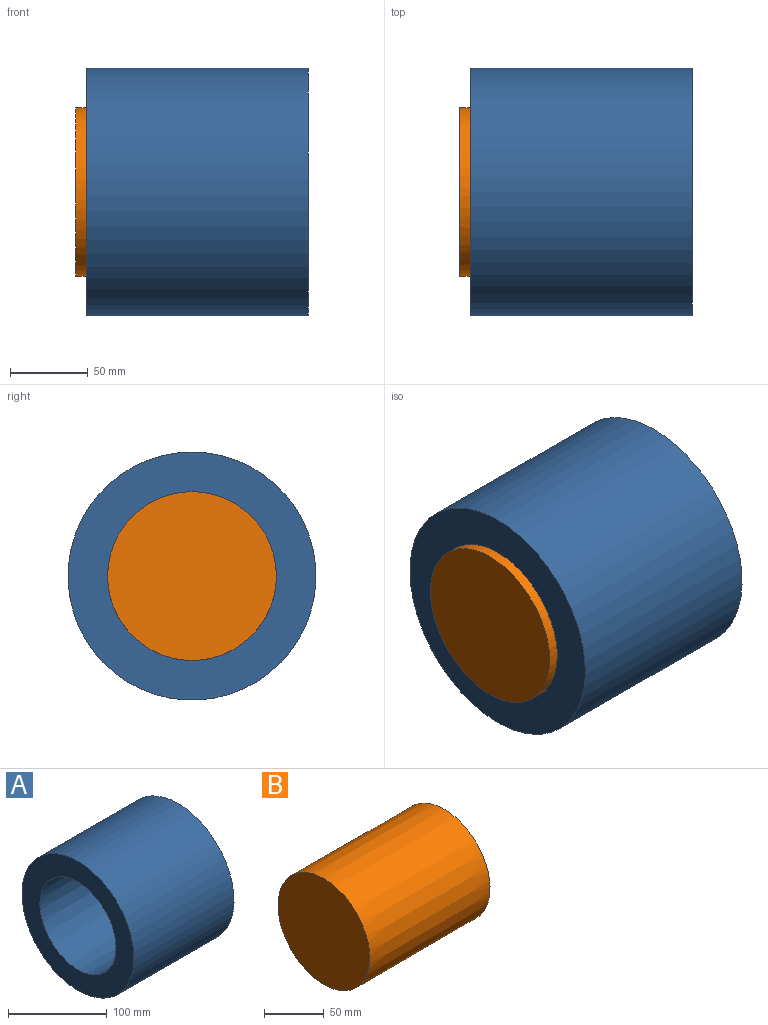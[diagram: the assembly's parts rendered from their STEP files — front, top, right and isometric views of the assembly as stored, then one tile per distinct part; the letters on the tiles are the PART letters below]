
ASSEMBLY  parts=2 mates=1
PART A: 5 faces, bbox 143x160x160 mm
  f0: cylinder r=80mm len=160mm, axis (-1,0,0), area 71879.6mm2, adj f1,f3
  f1: plane 160x160mm, normal (-1,0,0), area 10806.5mm2, adj f0,f2
  f2: cone r=53.93mm half-angle=0.2deg, axis (-1,0,0), area 47993.3mm2, adj f1,f4
  f3: plane 160x160mm, normal (1,0,0), area 10278.4mm2, adj f0,f4
  f4: cone r=55.93mm half-angle=44.9deg, axis (1,0,0), area 974.6mm2, adj f2,f3
PART B: 11 faces, bbox 143x108.8x108.8 mm
  f0: plane 108.83x108.83mm, normal (-1,0,0), area 9301.9mm2, adj f2
  f1: plane 107.91x107.91mm, normal (1,0,0), area 8831.1mm2, adj f2,f3,f5,f7,f9
  f2: cone r=54.41mm half-angle=0.2deg, axis (-1,0,0), area 48684.1mm2, adj f0,f1
  f3: cylinder r=5mm len=30mm, axis (1,0,0), area 942.5mm2, adj f1,f4
  f4: plane 10x10mm, normal (1,0,0), area 78.5mm2, adj f3
  f5: cylinder r=5mm len=30mm, axis (1,0,0), area 942.5mm2, adj f1,f6
  f6: plane 10x10mm, normal (1,0,0), area 78.5mm2, adj f5
  f7: cylinder r=5mm len=30mm, axis (1,0,0), area 942.5mm2, adj f1,f8
  f8: plane 10x10mm, normal (1,0,0), area 78.5mm2, adj f7
  f9: cylinder r=5mm len=30mm, axis (1,0,0), area 942.5mm2, adj f1,f10
  f10: plane 10x10mm, normal (1,0,0), area 78.5mm2, adj f9
PLACE A at identity
PLACE B t=(-6.9,0,0)mm
MATE slider B.f2 <-> A.f0  axis (1,0,0) through (136.1,0,0)mm
